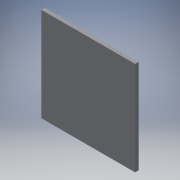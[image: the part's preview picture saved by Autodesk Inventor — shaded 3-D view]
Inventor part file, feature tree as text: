
AUTODESK INVENTOR PART (.ipt)
format: ipt  version: 2019 (Build 230136000, 136)  size: 90,624 bytes
history: native  units: in
note: dims shown in document units (in); Inventor stores cm internally (conversion verified against a paired STEP export)
features: other x3, extrude x1, sketch x1, reference x1
ambient origin geometry x8: Origin, YZ Plane, XZ Plane, XY Plane, X Axis, Y Axis, Z Axis, Center Point
bodies: Solid1 (feature_tree)
feature tree (6):
  extrude  "Extrusion1"  Depth=13.0in
  sketch  "Sketch1"  dims[d0=13.0in d1=13.0in d2=0.5in d3=0.0in]
  reference  "Reference1"
  other  "<userpath>\Desktop\Roombotics\UpperLevel.iam"
  other  "UpperLevel.iam"
  other  "Top:1"
